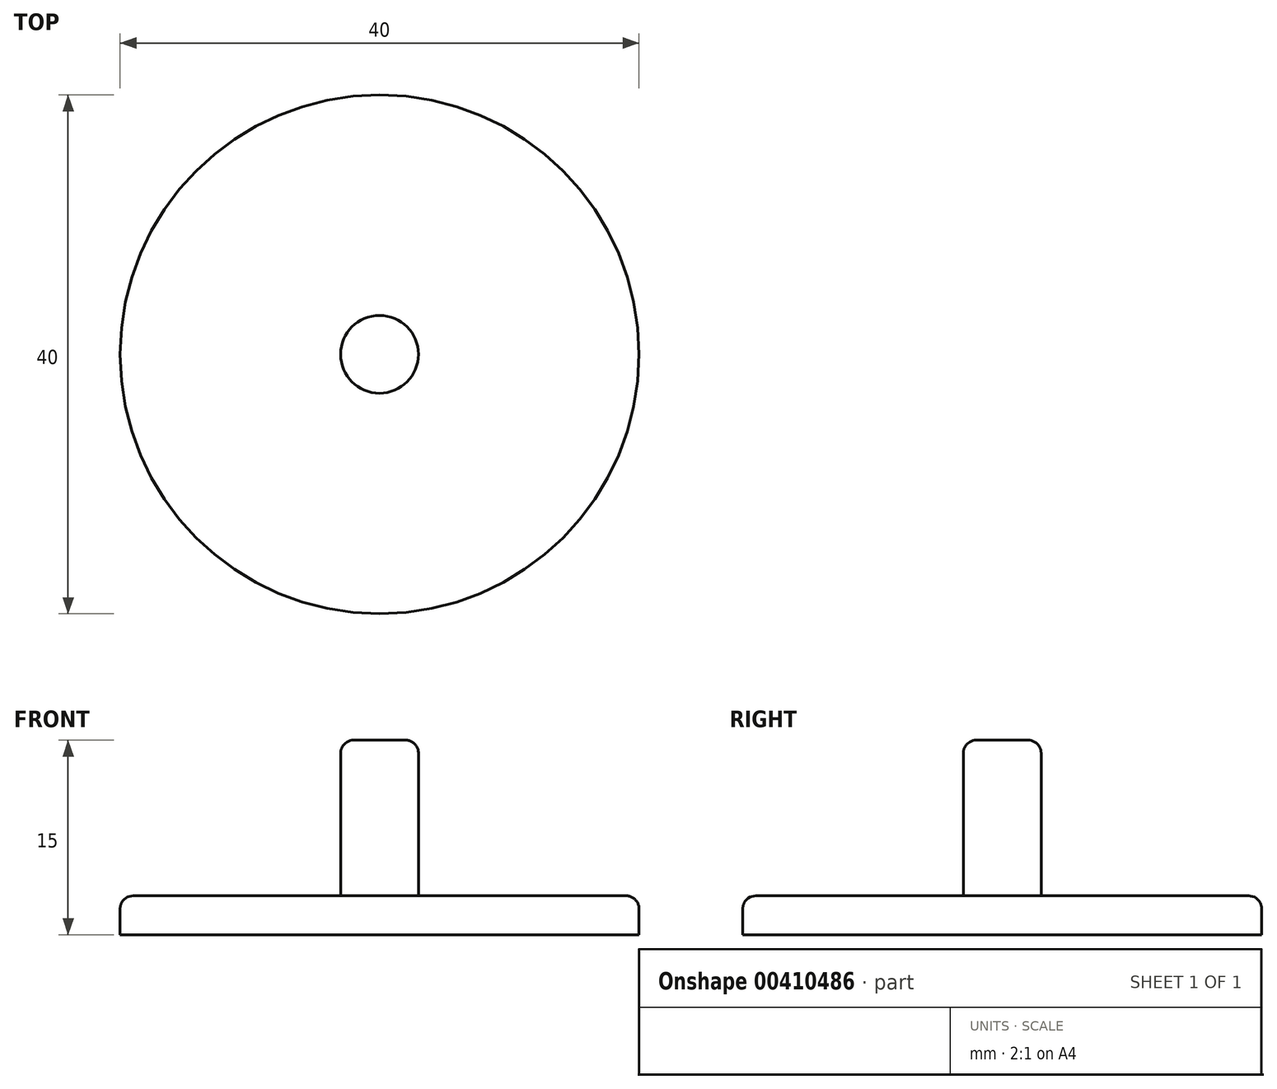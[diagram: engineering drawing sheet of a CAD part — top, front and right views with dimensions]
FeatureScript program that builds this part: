
annotation { "Feature Type Name" : "Feature", "Feature Type Description" : "" }
export const myFeature = defineFeature(function(context is Context, id is Id, definition is map)
    precondition{}
    {
        {
            var Q0;
            Q0=qCreatedBy(makeId("Top.planeOp"),FACE);
            var sketch = newSketch(context, id + "F0", { "sketchPlane" : qUnion([Q0])});
            skCircle(sketch, "E0", {"center": v(0, 0) * mm, "radius": 20 * mm});
            skSolve(sketch);
        }
        {
            var Q0;
            Q0=makeQuery(id+"F0.imprint","IMPRINT",FACE,{"disambiguationData":[TD([[makeQuery(id+"F0.imprint","IMPRINT",EDGE,{"derivedFrom":sQuery(id+"F0.wireOp",EDGE,"E0")}),1.0]])]});
            extrude(context, id + "F1", {"entities" : qUnion([Q0]), "oppositeDirection" : true, "depth" : 3 * mm, "offsetDistance" : 25 * mm});
        }
        {
            var Q0;
            Q0=makeQuery(id+"F1.opExtrude","CAP_FACE",FACE,{"disambiguationData":[OSD([sQuery(id+"F0.wireOp",EDGE,"E0")])],"isStart":true});
            var sketch = newSketch(context, id + "F2", { "sketchPlane" : qUnion([Q0])});
            skCircle(sketch, "E1", {"center": v(0, 0) * mm, "radius": 3 * mm});
            skSolve(sketch);
        }
        {
            var Q0;
            Q0=makeQuery(id+"F2.imprint","IMPRINT",FACE,{"disambiguationData":[TD([[makeQuery(id+"F2.imprint","IMPRINT",EDGE,{"derivedFrom":sQuery(id+"F2.wireOp",EDGE,"E1")}),1.0]])]});
            extrude(context, id + "F3", {"entities" : qUnion([Q0]), "operationType" : NewBodyOperationType.ADD, "depth" : 12 * mm, "offsetDistance" : 25 * mm});
        }
        {
            var Q0;
            Q0=makeQuery(id+"F1.opExtrude","CAP_EDGE",EDGE,{"disambiguationData":[OSD([sQuery(id+"F0.wireOp",EDGE,"E0")])],"isStart":true});
            var Q1;
            Q1=makeQuery(id+"F3.opExtrude","CAP_EDGE",EDGE,{"disambiguationData":[OSD([sQuery(id+"F2.wireOp",EDGE,"E1")])],"isStart":false});
            var Q2;
            Q2=makeQuery(id+"F3.opExtrude","CAP_EDGE",EDGE,{"disambiguationData":[OSD([sQuery(id+"F2.wireOp",EDGE,"E1")])],"isStart":true});
            fillet(context, id + "F4", {"entities" : qUnion([Q0, Q1, Q2]), "radius" : 1 * mm, "tangentPropagation" : true, "allowEdgeOverflow" : false});
        }
    });
